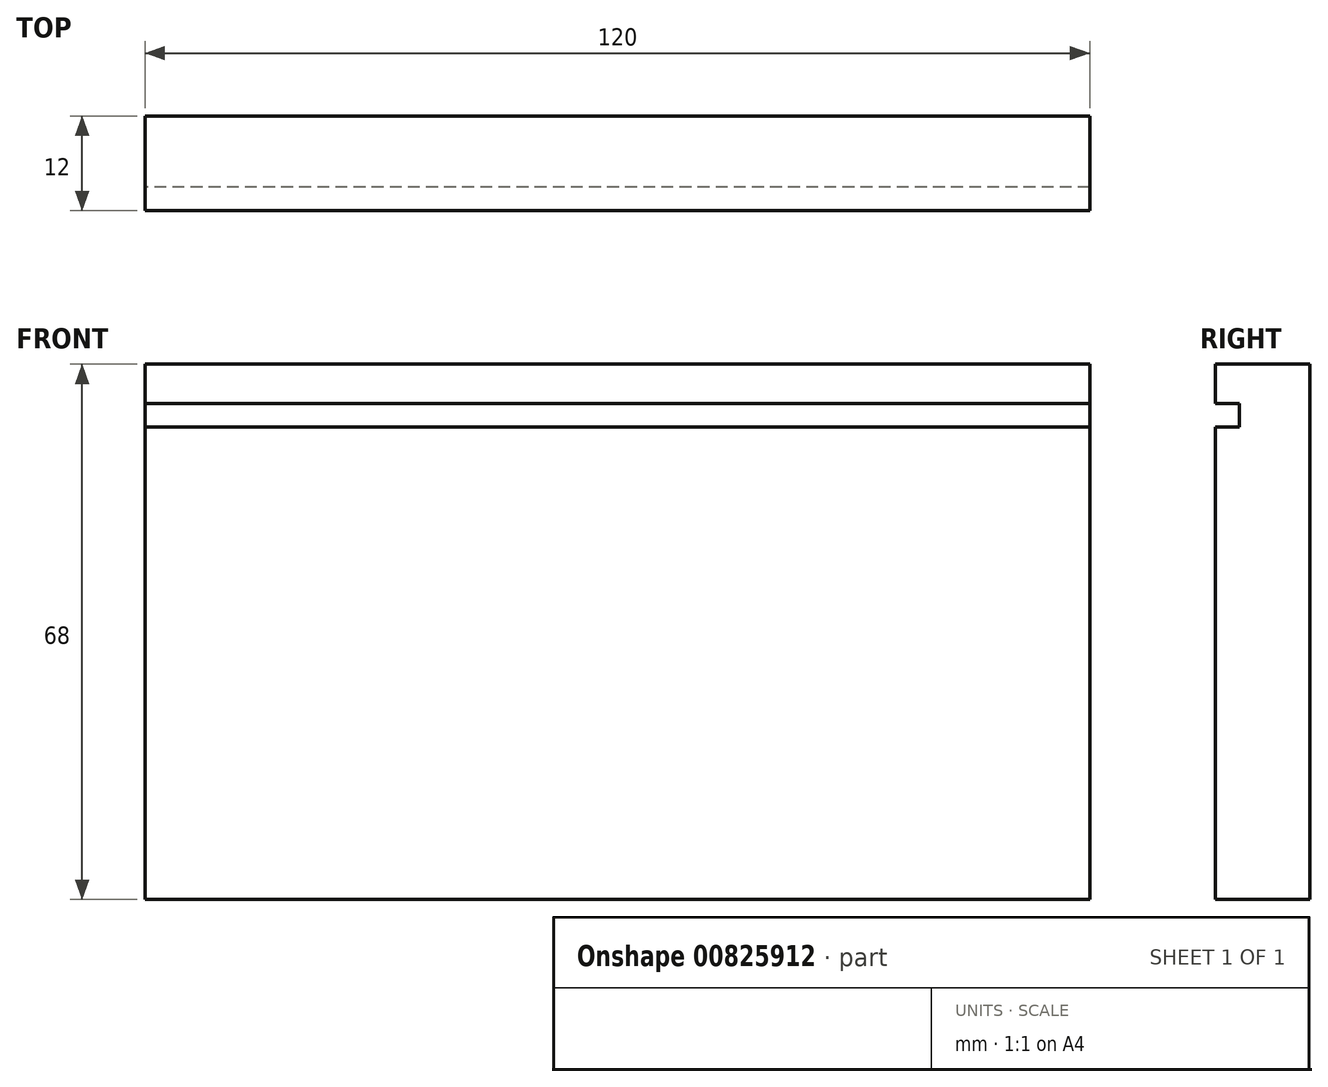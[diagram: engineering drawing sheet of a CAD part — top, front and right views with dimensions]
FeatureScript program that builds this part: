
annotation { "Feature Type Name" : "Feature", "Feature Type Description" : "" }
export const myFeature = defineFeature(function(context is Context, id is Id, definition is map)
    precondition{}
    {
        {
            var Q0;
            Q0=qCreatedBy(makeId("Right.planeOp"),FACE);
            var sketch = newSketch(context, id + "F0", { "sketchPlane" : qUnion([Q0])});
            skLineSegment(sketch, "E0.bottom", {"start": v(2.4, 0) * mm, "end": v(14.4, 0) * mm});
            skLineSegment(sketch, "E0.top", {"start": v(2.4, 68) * mm, "end": v(14.4, 68) * mm});
            skLineSegment(sketch, "E0.left", {"start": v(2.4, 0) * mm, "end": v(2.4, 60) * mm});
            skLineSegment(sketch, "E0.right", {"start": v(14.4, 0) * mm, "end": v(14.4, 68) * mm});
            skLineSegment(sketch, "E1", {"start": v(2.4, 60) * mm, "end": v(5.4, 60) * mm});
            skLineSegment(sketch, "E2", {"start": v(5.4, 60) * mm, "end": v(5.4, 63) * mm});
            skLineSegment(sketch, "E3", {"start": v(5.4, 63) * mm, "end": v(2.4, 63) * mm});
            skLineSegment(sketch, "E4.trimOffspring", {"start": v(2.4, 63) * mm, "end": v(2.4, 68) * mm});
            skSolve(sketch);
        }
        {
            var Q0;
            Q0 = qSketchRegion(id + "F0", true);
            extrude(context, id + "F1", {"entities" : qUnion([Q0]), "depth" : 120 * mm, "offsetDistance" : 25 * mm});
        }
    });
